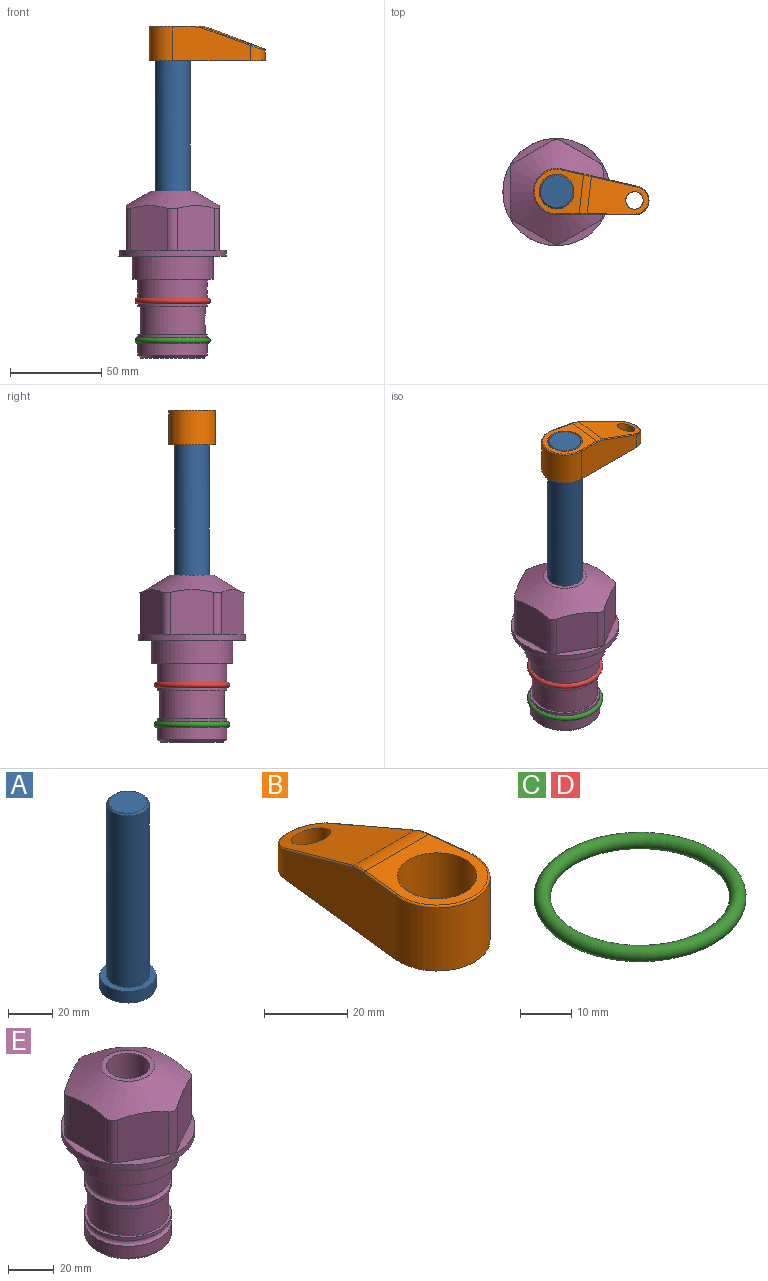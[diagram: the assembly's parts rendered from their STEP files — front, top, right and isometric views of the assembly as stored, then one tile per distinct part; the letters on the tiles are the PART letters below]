
ASSEMBLY  parts=5 mates=3
PART A: 6 faces, bbox 25.4x25.4x101.6 mm
  f0: plane 17.46x17.46mm, normal (0,0,1), area 239.5mm2, adj f5
  f1: plane 25.4x25.4mm, normal (0,0,-1), area 506.7mm2, adj f2
  f2: cylinder r=12.7mm len=25.4mm, axis (0,0,1), area 506.7mm2, adj f1,f3
  f3: plane 25.4x25.4mm, normal (0,0,1), area 221.7mm2, adj f2,f4
  f4: cylinder r=9.53mm len=94.46mm, axis (0,0,1), area 5653mm2, adj f3,f5
  f5: cone r=8.73mm half-angle=45deg, axis (0,0,-1), area 64.4mm2, adj f0,f4
PART B: 44 faces, bbox 27.5x64.5x19.1 mm
  f0: plane 2.3x0.95mm, normal (0,0,-1), area 1mm2, adj f25,f30,f34
  f1: plane 63.5x25.4mm, normal (0,0,-1), area 561.7mm2, adj f2,f3,f4,f5,f6,f7,f19,f20
  f2: cylinder r=12.7mm len=25.4mm, axis (0,0,-1), area 792.2mm2, adj f1,f3,f5,f13
  f3: plane 42.33x18.54mm, normal (0.99,0.11,0), area 647mm2, adj f1,f2,f4,f11,f12,f14
  f4: cylinder r=7.94mm len=15.78mm, axis (0,0,-1), area 158.6mm2, adj f1,f3,f5,f16
  f5: plane 42.33x18.54mm, normal (-0.99,0.11,0), area 647mm2, adj f1,f2,f4,f15,f17,f18
  f6: cylinder r=9.53mm len=19.05mm, axis (0,0,-1), area 1140.1mm2, adj f1,f8
  f7: cylinder r=4.76mm len=10.98mm, axis (0,0,-1), area 276.1mm2, adj f1,f9
  f8: plane 25.83x24.38mm, normal (0,0,1), area 262.2mm2, adj f6,f10,f11,f13,f15
  f9: plane 32.49x20.55mm, normal (0,0.34,0.94), area 489.9mm2, adj f7,f10,f14,f16,f18
  f10: cylinder r=12.7mm len=21.49mm, axis (-1,0,0), area 93.2mm2, adj f8,f9,f12,f17
  f11: cylinder r=0.51mm len=12.34mm, axis (0.11,-0.99,0), area 9.9mm2, adj f3,f8,f12,f13
  f12: bspline ~7.62x1.64mm, area 3.5mm2, adj f3,f10,f11,f14
  f13: torus R=12.19mm, axis (0,0,1), area 33.6mm2, adj f2,f8,f11,f15
  f14: cylinder r=0.51mm len=26.01mm, axis (0.1,-0.93,0.34), area 21.6mm2, adj f3,f9,f12,f16
  f15: cylinder r=0.51mm len=12.34mm, axis (0.11,0.99,0), area 9.9mm2, adj f5,f8,f13,f17
  f16: bspline ~15.78x7.05mm, area 15.7mm2, adj f4,f9,f14,f18
  f17: bspline ~7.62x1.64mm, area 3.5mm2, adj f5,f10,f15,f18
  f18: cylinder r=0.51mm len=26.01mm, axis (0.1,0.93,-0.34), area 21.6mm2, adj f5,f9,f16,f17
  f19: plane 21.6x14.29mm, normal (-0.99,-0.11,0), area 242.6mm2, adj f1,f26,f28,f34,f36,f38
  f20: plane 21.6x14.29mm, normal (0.99,-0.11,0), area 242.6mm2, adj f1,f27,f29,f37,f39,f41
  f21: cylinder r=12.7mm len=14.29mm, axis (0,0,-1), area 173.2mm2, adj f1,f26,f27,f30,f31,f33
  f22: cylinder r=7.94mm len=7.63mm, axis (0,0,-1), area 53.8mm2, adj f1,f28,f29,f42
  f23: plane 2.3x0.95mm, normal (0,0,-1), area 1mm2, adj f25,f33,f37
  f24: plane 17.94x12.32mm, normal (0,-0.34,-0.94), area 191.2mm2, adj f25,f38,f41,f42
  f25: cylinder r=9.53mm len=12.93mm, axis (-1,0,0), area 37.5mm2, adj f0,f23,f24,f31,f36,f39
  f26: cylinder r=1.59mm len=14.29mm, axis (0,0,-1), area 49mm2, adj f1,f19,f21,f32
  f27: cylinder r=1.59mm len=14.29mm, axis (0,0,-1), area 49mm2, adj f1,f20,f21,f35
  f28: cylinder r=1.59mm len=7.28mm, axis (0,0,-1), area 22.1mm2, adj f1,f19,f22,f40
  f29: cylinder r=1.59mm len=7.28mm, axis (0,0,-1), area 22.1mm2, adj f1,f20,f22,f43
  f30: torus R=14.29mm, axis (0,0,1), area 5.8mm2, adj f0,f21,f31,f32
  f31: bspline ~11.06x2.73mm, area 20.8mm2, adj f21,f25,f30,f33
  f32: sphere r=1.59mm, area 5.4mm2, adj f26,f30,f34
  f33: torus R=14.29mm, axis (0,0,1), area 5.8mm2, adj f21,f23,f31,f35
  f34: cylinder r=1.59mm len=1.68mm, axis (-0.11,0.99,0), area 2.4mm2, adj f0,f19,f32,f36
  f35: sphere r=1.59mm, area 5.4mm2, adj f27,f33,f37
  f36: bspline ~5.82x2.33mm, area 7.7mm2, adj f19,f25,f34,f38
  f37: cylinder r=1.59mm len=1.68mm, axis (0.11,0.99,0), area 2.4mm2, adj f20,f23,f35,f39
  f38: cylinder r=1.59mm len=18.33mm, axis (0.1,-0.93,0.34), area 46.7mm2, adj f19,f24,f36,f40
  f39: bspline ~5.82x2.33mm, area 7.7mm2, adj f20,f25,f37,f41
  f40: sphere r=1.59mm, area 3.6mm2, adj f28,f38,f42
  f41: cylinder r=1.59mm len=18.33mm, axis (0.1,0.93,-0.34), area 46.7mm2, adj f20,f24,f39,f43
  f42: bspline ~8.31x1.84mm, area 15.3mm2, adj f22,f24,f40,f43
  f43: sphere r=1.59mm, area 3.6mm2, adj f29,f41,f42
PART C: 1 faces, bbox 44.7x44.7x3.2 mm
  f0: torus R=19.05mm, axis (0,0,1), area 1193.9mm2
PART D: same geometry as C
PART E: 36 faces, bbox 58.7x58.7x91.2 mm
  f0: cylinder r=17.78mm len=35.56mm, axis (0,0,1), area 1670.8mm2, adj f23,f24,f31
  f1: cylinder r=19.05mm len=38.1mm, axis (0,0,1), area 1191.9mm2, adj f26,f27,f30
  f2: plane 58.66x58.66mm, normal (0,0,-1), area 1150.6mm2, adj f3,f28
  f3: cylinder r=29.33mm len=58.66mm, axis (0,0,-1), area 585.1mm2, adj f2,f4
  f4: plane 58.66x58.66mm, normal (0,0,1), area 475.9mm2, adj f3,f5,f6,f7,f8,f9,f10,f11
  f5: plane 24.5x20.32mm, normal (-0.5,0.87,0), area 562.8mm2, adj f4,f15,f16,f17
  f6: plane 24.5x20.32mm, normal (0.5,0.87,0), area 562.8mm2, adj f4,f14,f15,f17
  f7: plane 24.5x23.48mm, normal (1,0,0), area 562.8mm2, adj f4,f13,f14,f17
  f8: plane 24.5x20.32mm, normal (0.5,-0.87,0), area 562.8mm2, adj f4,f12,f13,f17
  f9: plane 24.5x20.32mm, normal (-0.5,-0.87,0), area 562.8mm2, adj f4,f11,f12,f17
  f10: plane 24.5x23.48mm, normal (-1,0,0), area 562.8mm2, adj f4,f11,f16,f17
  f11: cylinder r=5.08mm len=23.01mm, axis (0,0,-1), area 121.2mm2, adj f4,f9,f10,f17
  f12: cylinder r=5.08mm len=23.01mm, axis (0,0,-1), area 121.2mm2, adj f4,f8,f9,f17
  f13: cylinder r=5.08mm len=23.01mm, axis (0,0,-1), area 121.2mm2, adj f4,f7,f8,f17
  f14: cylinder r=5.08mm len=23.01mm, axis (0,0,-1), area 121.2mm2, adj f4,f6,f7,f17
  f15: cylinder r=5.08mm len=23.01mm, axis (0,0,-1), area 121.2mm2, adj f4,f5,f6,f17
  f16: cylinder r=5.08mm len=23.01mm, axis (0,0,-1), area 121.2mm2, adj f4,f5,f10,f17
  f17: cone r=11.73mm half-angle=60deg, axis (0,0,-1), area 2071.8mm2, adj f5,f6,f7,f8,f9,f10,f11,f12
  f18: plane 23.46x23.46mm, normal (0,0,1), area 147.4mm2, adj f17,f35
  f19: plane 34.93x34.93mm, normal (0,0,-1), area 958mm2, adj f29
  f20: cylinder r=19.05mm len=38.1mm, axis (0,0,1), area 760.1mm2, adj f21,f29
  f21: torus R=19.05mm, axis (0,0,1), area 565.3mm2, adj f20,f22
  f22: cylinder r=19.05mm len=38.1mm, axis (0,0,1), area 190mm2, adj f21,f23
  f23: plane 38.1x38.1mm, normal (0,0,1), area 146.9mm2, adj f0,f22
  f24: plane 38.1x38.1mm, normal (0,0,-1), area 146.9mm2, adj f0,f25
  f25: cylinder r=19.05mm len=38.1mm, axis (0,0,1), area 190mm2, adj f24,f26
  f26: torus R=19.05mm, axis (0,0,1), area 565.3mm2, adj f1,f25
  f27: plane 44.45x44.45mm, normal (0,0,-1), area 411.7mm2, adj f1,f28
  f28: cylinder r=22.23mm len=44.45mm, axis (0,0,1), area 1773.5mm2, adj f2,f27
  f29: cone r=19.05mm half-angle=45deg, axis (0,0,1), area 257.5mm2, adj f19,f20
  f30: cylinder r=3.17mm len=6.75mm, axis (-1,0,0), area 128mm2, adj f1,f33
  f31: cylinder r=3.17mm len=6.35mm, axis (-1,0,0), area 102.5mm2, adj f0,f33
  f32: plane 25.4x25.4mm, normal (0,0,1), area 506.7mm2, adj f33
  f33: cylinder r=12.7mm len=66.42mm, axis (0,0,-1), area 5236.2mm2, adj f30,f31,f32,f34
  f34: cone r=9.53mm half-angle=30deg, axis (0,0,-1), area 443.4mm2, adj f33,f35
  f35: cylinder r=9.53mm len=19.05mm, axis (0,0,-1), area 849mm2, adj f18,f34
PLACE A rot(axis=(0,0,-1),6.4deg) t=(0,0,52.18)mm
PLACE B rot(axis=(0,0,-1),96.4deg) t=(0,0,106.79)mm
PLACE C t=(0,0,-21.59)mm
PLACE D at identity
PLACE E at identity fixed
MATE fastened C.f0 <-> E.f0  axis (0,0,1) through (0,0,-46.1)mm
MATE cylindrical A.f2 <-> E.f0  axis (0,0,1) through (0,0,77.82)mm
MATE fastened B.f2 <-> A.f2  axis (0,0,1) through (0,0,125.84)mm
